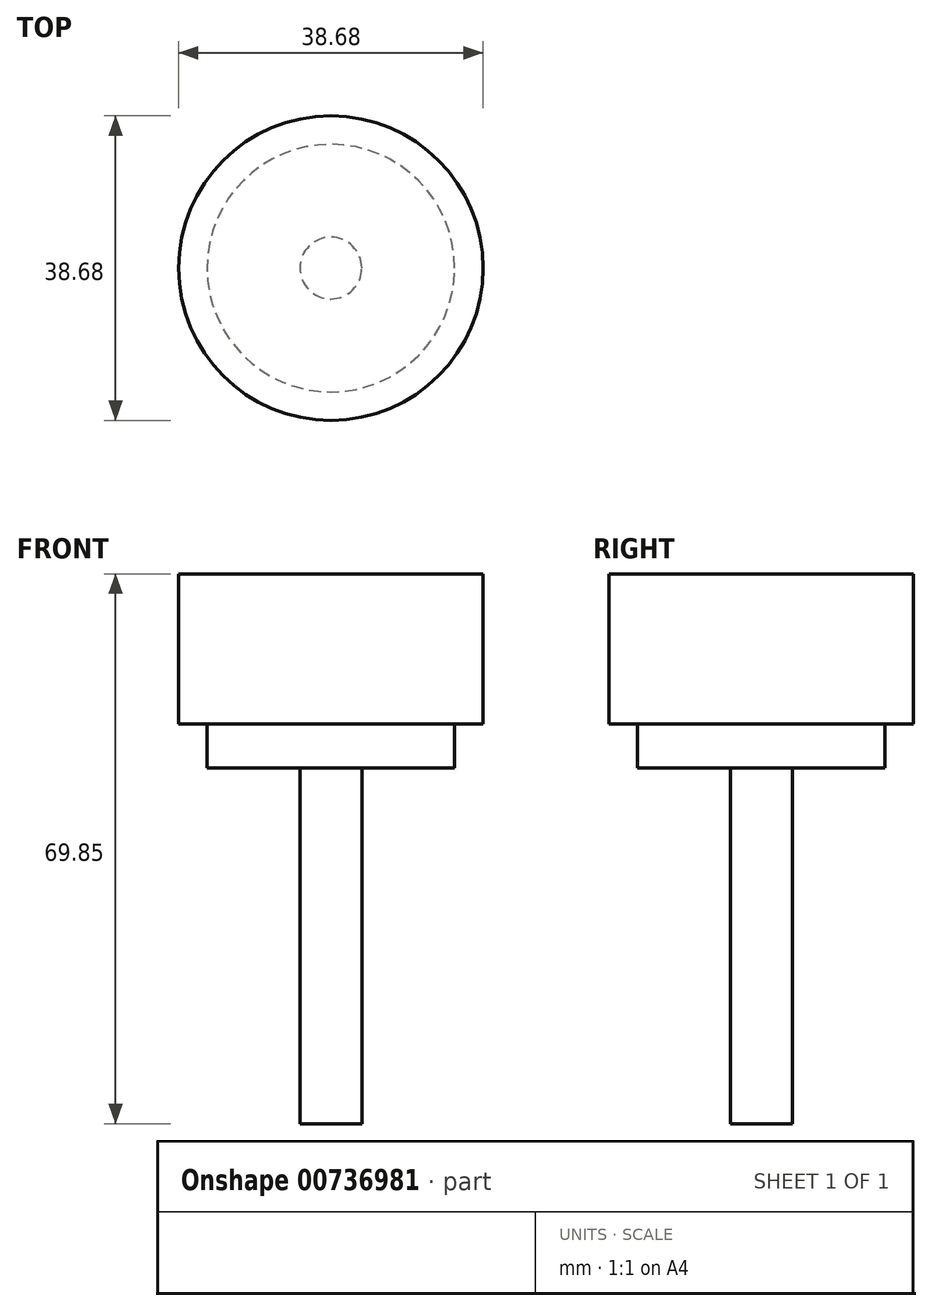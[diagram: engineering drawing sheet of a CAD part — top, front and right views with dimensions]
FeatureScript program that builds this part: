
annotation { "Feature Type Name" : "Feature", "Feature Type Description" : "" }
export const myFeature = defineFeature(function(context is Context, id is Id, definition is map)
    precondition{}
    {
        {
            var Q0;
            Q0=qCreatedBy(makeId("Front.planeOp"),FACE);
            var sketch = newSketch(context, id + "F0", { "sketchPlane" : qUnion([Q0])});
            skLineSegment(sketch, "E0", {"start": v(0, 42.02) * mm, "end": v(0, -41.69) * mm, "construction": true});
            skLineSegment(sketch, "E1", {"start": v(0, 0) * mm, "end": v(19.34, 0) * mm});
            skLineSegment(sketch, "E2", {"start": v(19.34, 0) * mm, "end": v(19.34, -19.05) * mm});
            skLineSegment(sketch, "E3", {"start": v(19.34, -19.05) * mm, "end": v(15.72, -19.05) * mm});
            skLineSegment(sketch, "E4", {"start": v(15.72, -19.05) * mm, "end": v(15.72, -24.69) * mm});
            skLineSegment(sketch, "E5", {"start": v(15.72, -24.69) * mm, "end": v(3.92, -24.69) * mm});
            skLineSegment(sketch, "E6", {"start": v(3.92, -24.69) * mm, "end": v(3.92, -69.85) * mm});
            skLineSegment(sketch, "E7", {"start": v(3.92, -69.85) * mm, "end": v(0, -69.85) * mm});
            skLineSegment(sketch, "E8", {"start": v(0, 0) * mm, "end": v(0, -69.85) * mm});
            skSolve(sketch);
        }
        {
            var Q0;
            Q0 = qSketchRegion(id + "F0", true);
            var Q1;
            Q1=sQuery(id+"F0.wireOp",EDGE,"E0");
            revolve(context, id + "F1", {"surfaceOperationType" : NewSurfaceOperationType.NEW, "entities" : qUnion([Q0]), "axis" : qUnion([Q1]), "revolveType" : RevolveType.FULL});
        }
    });
